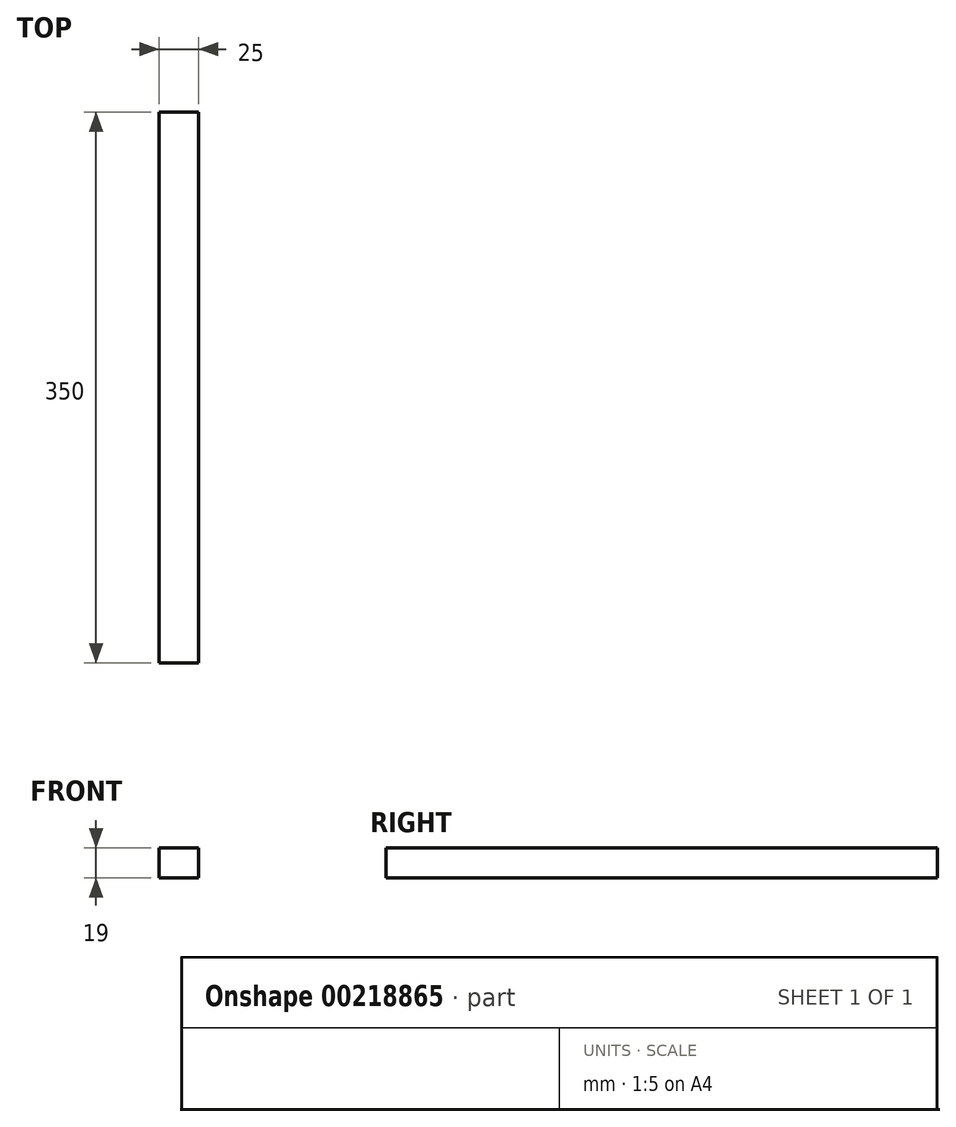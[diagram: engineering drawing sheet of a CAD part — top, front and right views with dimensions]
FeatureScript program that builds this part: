
annotation { "Feature Type Name" : "Feature", "Feature Type Description" : "" }
export const myFeature = defineFeature(function(context is Context, id is Id, definition is map)
    precondition{}
    {
        {
            var Q0;
            Q0=qCreatedBy(makeId("Right.planeOp"),FACE);
            var sketch = newSketch(context, id + "F0", { "sketchPlane" : qUnion([Q0])});
            skLineSegment(sketch, "E0.bottom", {"start": v(-126.67, 19) * mm, "end": v(223.33, 19) * mm});
            skLineSegment(sketch, "E0.top", {"start": v(-126.67, 0) * mm, "end": v(223.33, 0) * mm});
            skLineSegment(sketch, "E0.left", {"start": v(-126.67, 19) * mm, "end": v(-126.67, 0) * mm});
            skLineSegment(sketch, "E0.right", {"start": v(223.33, 19) * mm, "end": v(223.33, 0) * mm});
            skSolve(sketch);
        }
        {
            var Q0;
            Q0 = qSketchRegion(id + "F0", true);
            extrude(context, id + "F1", {"entities" : qUnion([Q0]), "depth" : 25 * mm});
        }
    });
